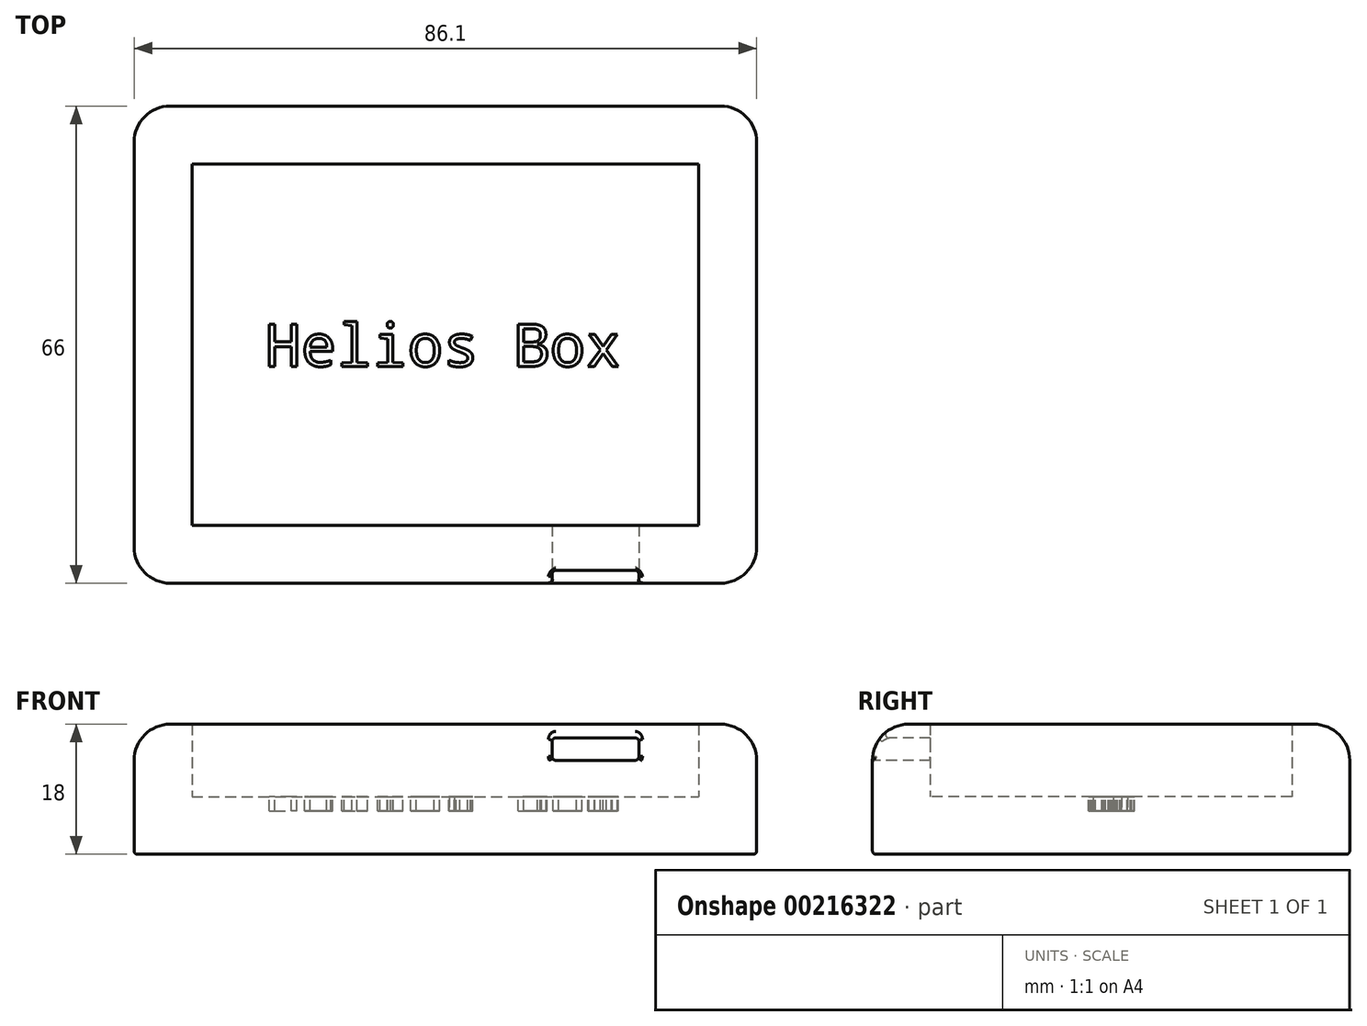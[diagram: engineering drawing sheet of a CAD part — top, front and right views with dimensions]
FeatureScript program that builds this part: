
annotation { "Feature Type Name" : "Feature", "Feature Type Description" : "" }
export const myFeature = defineFeature(function(context is Context, id is Id, definition is map)
    precondition{}
    {
        {
            var Q0;
            Q0=qCreatedBy(makeId("Top.planeOp"),FACE);
            var sketch = newSketch(context, id + "F0", { "sketchPlane" : qUnion([Q0])});
            skLineSegment(sketch, "E0.bottom", {"start": v(-35.05, 25) * mm, "end": v(35.05, 25) * mm});
            skLineSegment(sketch, "E0.top", {"start": v(-35.05, -25) * mm, "end": v(35.05, -25) * mm});
            skLineSegment(sketch, "E0.left", {"start": v(-35.05, 25) * mm, "end": v(-35.05, -25) * mm});
            skLineSegment(sketch, "E0.right", {"start": v(35.05, 25) * mm, "end": v(35.05, -25) * mm});
            skLineSegment(sketch, "E1.bottom", {"start": v(-43.05, 33) * mm, "end": v(43.05, 33) * mm});
            skLineSegment(sketch, "E1.top", {"start": v(-43.05, -33) * mm, "end": v(43.05, -33) * mm});
            skLineSegment(sketch, "E1.left", {"start": v(-43.05, 33) * mm, "end": v(-43.05, -33) * mm});
            skLineSegment(sketch, "E1.right", {"start": v(43.05, 33) * mm, "end": v(43.05, -33) * mm});
            skSolve(sketch);
        }
        {
            var Q0;
            Q0=makeQuery(id+"F0.imprint","IMPRINT",FACE,{"disambiguationData":[TD([[makeQuery(id+"F0.imprint","IMPRINT",EDGE,{"derivedFrom":sQuery(id+"F0.wireOp",EDGE,"E0.bottom")}),-1.0]])]});
            extrude(context, id + "F1", {"entities" : qUnion([Q0]), "depth" : 8 * mm});
        }
        {
            var Q0;
            Q0=makeQuery(id+"F0.imprint","IMPRINT",FACE,{"disambiguationData":[TD([[makeQuery(id+"F0.imprint","IMPRINT",EDGE,{"derivedFrom":sQuery(id+"F0.wireOp",EDGE,"E0.bottom")}),1.0]])]});
            extrude(context, id + "F2", {"entities" : qUnion([Q0]), "operationType" : NewBodyOperationType.ADD, "depth" : 18 * mm});
        }
        {
            var Q0;
            Q0=makeQuery(id+"F2.opExtrude","SWEPT_EDGE",EDGE,{"disambiguationData":[OSD([sQuery(id+"F0.wireOp",EDGE,"E1.top"),sQuery(id+"F0.wireOp",EDGE,"E1.left")])]});
            var Q1;
            Q1=makeQuery(id+"F2.opExtrude","CAP_EDGE",EDGE,{"disambiguationData":[OSD([sQuery(id+"F0.wireOp",EDGE,"E1.top")])],"isStart":false});
            var Q2;
            Q2=makeQuery(id+"F2.opExtrude","CAP_EDGE",EDGE,{"disambiguationData":[OSD([sQuery(id+"F0.wireOp",EDGE,"E1.left")])],"isStart":false});
            var Q3;
            Q3=makeQuery(id+"F2.opExtrude","SWEPT_EDGE",EDGE,{"disambiguationData":[OSD([sQuery(id+"F0.wireOp",EDGE,"E1.top"),sQuery(id+"F0.wireOp",EDGE,"E1.right")])]});
            var Q4;
            Q4=makeQuery(id+"F2.opExtrude","CAP_EDGE",EDGE,{"disambiguationData":[OSD([sQuery(id+"F0.wireOp",EDGE,"E1.right")])],"isStart":false});
            var Q5;
            Q5=makeQuery(id+"F2.opExtrude","SWEPT_EDGE",EDGE,{"disambiguationData":[OSD([sQuery(id+"F0.wireOp",EDGE,"E1.bottom"),sQuery(id+"F0.wireOp",EDGE,"E1.right")])]});
            var Q6;
            Q6=makeQuery(id+"F2.opExtrude","CAP_EDGE",EDGE,{"disambiguationData":[OSD([sQuery(id+"F0.wireOp",EDGE,"E1.bottom")])],"isStart":false});
            var Q7;
            Q7=makeQuery(id+"F2.opExtrude","SWEPT_EDGE",EDGE,{"disambiguationData":[OSD([sQuery(id+"F0.wireOp",EDGE,"E1.bottom"),sQuery(id+"F0.wireOp",EDGE,"E1.left")])]});
            fillet(context, id + "F3", {"entities" : qUnion([Q0, Q1, Q2, Q3, Q4, Q5, Q6, Q7]), "radius" : 5 * mm, "tangentPropagation" : true, "allowEdgeOverflow" : false});
        }
        {
            var Q0;
            Q0=makeQuery(id+"F2.opExtrude","SWEPT_FACE",FACE,{"disambiguationData":[OSD([sQuery(id+"F0.wireOp",EDGE,"E1.top")])]});
            var sketch = newSketch(context, id + "F4", { "sketchPlane" : qUnion([Q0])});
            skLineSegment(sketch, "E2.bottom", {"start": v(14.75, 16.1) * mm, "end": v(26.75, 16.1) * mm});
            skLineSegment(sketch, "E2.top", {"start": v(14.75, 10.6) * mm, "end": v(26.75, 10.6) * mm});
            skLineSegment(sketch, "E2.left", {"start": v(14.75, 16.1) * mm, "end": v(14.75, 10.6) * mm});
            skLineSegment(sketch, "E2.right", {"start": v(26.75, 16.1) * mm, "end": v(26.75, 10.6) * mm});
            skSolve(sketch);
        }
        {
            var Q0;
            Q0=makeQuery(id+"F4.imprint","IMPRINT",FACE,{"disambiguationData":[TD([[makeQuery(id+"F4.imprint","IMPRINT",EDGE,{"derivedFrom":sQuery(id+"F4.wireOp",EDGE,"E2.bottom")}),-1.0]])]});
            extrude(context, id + "F5", {"entities" : qUnion([Q0]), "operationType" : NewBodyOperationType.REMOVE, "oppositeDirection" : true, "depth" : 8 * mm});
        }
        {
            var Q0;
            Q0=makeQuery(id+"F5.boolean.opBoolean","INTERSECT",EDGE,{"derivedFrom":[makeQuery(id+"F3.opFillet","BLEND_FACE",FACE,{"disambiguationData":[OSD([sQuery(id+"F0.wireOp",EDGE,"E1.top")])]}),makeQuery(id+"F5.opExtrude","SWEPT_FACE",FACE,{"disambiguationData":[OSD([sQuery(id+"F4.wireOp",EDGE,"E2.bottom")])]})]});
            var Q1;
            Q1=makeQuery(id+"F5.boolean.opBoolean","INTERSECT",EDGE,{"derivedFrom":[makeQuery(id+"F3.opFillet","BLEND_FACE",FACE,{"disambiguationData":[OSD([sQuery(id+"F0.wireOp",EDGE,"E1.top")])]}),makeQuery(id+"F5.opExtrude","SWEPT_FACE",FACE,{"disambiguationData":[OSD([sQuery(id+"F4.wireOp",EDGE,"E2.right")])]})]});
            var Q2;
            Q2=makeQuery(id+"F5.boolean.opBoolean","INTERSECT",EDGE,{"derivedFrom":[makeQuery(id+"F3.opFillet","BLEND_FACE",FACE,{"disambiguationData":[OSD([sQuery(id+"F0.wireOp",EDGE,"E1.top")])]}),makeQuery(id+"F5.opExtrude","SWEPT_FACE",FACE,{"disambiguationData":[OSD([sQuery(id+"F4.wireOp",EDGE,"E2.left")])]})]});
            var Q3;
            {var subQ0=sQuery(id+"F0.wireOp",EDGE,"E1.top");Q3=makeQuery(id+"F5.boolean.opBoolean","MERGE",EDGE,{"derivedFrom":[makeQuery(id+"F3.opFillet","BLEND_EDGE",EDGE,{"blendedFrom":[makeQuery(id+"F2.opExtrude","CAP_EDGE",EDGE,{"disambiguationData":[OSD([subQ0])],"isStart":false}),makeQuery(id+"F2.opExtrude","SWEPT_FACE",FACE,{"disambiguationData":[OSD([subQ0])]})],"blendedInto":[makeQuery(id+"F2.opExtrude","SWEPT_FACE",FACE,{"disambiguationData":[OSD([subQ0])]})]}),makeQuery(id+"F5.opExtrude","CAP_EDGE",EDGE,{"disambiguationData":[OSD([subQ0])],"isStart":true})]});}
            var Q4;
            Q4=makeQuery(id+"F5.boolean.opBoolean","COPY",EDGE,{"derivedFrom":makeQuery(id+"F5.opExtrude","SWEPT_EDGE",EDGE,{"disambiguationData":[OSD([sQuery(id+"F4.wireOp",EDGE,"E2.bottom"),sQuery(id+"F4.wireOp",EDGE,"E2.right")])]})});
            var Q5;
            Q5=makeQuery(id+"F5.boolean.opBoolean","COPY",EDGE,{"derivedFrom":makeQuery(id+"F5.opExtrude","SWEPT_EDGE",EDGE,{"disambiguationData":[OSD([sQuery(id+"F0.wireOp",EDGE,"E1.top"),sQuery(id+"F4.wireOp",EDGE,"E2.right")])]})});
            var Q6;
            Q6=makeQuery(id+"F5.boolean.opBoolean","COPY",EDGE,{"derivedFrom":makeQuery(id+"F5.opExtrude","SWEPT_EDGE",EDGE,{"disambiguationData":[OSD([sQuery(id+"F0.wireOp",EDGE,"E1.top"),sQuery(id+"F4.wireOp",EDGE,"E2.left")])]})});
            var Q7;
            Q7=makeQuery(id+"F5.boolean.opBoolean","COPY",EDGE,{"derivedFrom":makeQuery(id+"F5.opExtrude","SWEPT_EDGE",EDGE,{"disambiguationData":[OSD([sQuery(id+"F4.wireOp",EDGE,"E2.bottom"),sQuery(id+"F4.wireOp",EDGE,"E2.left")])]})});
            var Q8;
            Q8=makeQuery(id+"F5.boolean.opBoolean","COPY",EDGE,{"derivedFrom":makeQuery(id+"F5.opExtrude","CAP_EDGE",EDGE,{"disambiguationData":[OSD([sQuery(id+"F0.wireOp",EDGE,"E1.top")])],"isStart":false})});
            var Q9;
            Q9=makeQuery(id+"F5.boolean.opBoolean","COPY",EDGE,{"derivedFrom":makeQuery(id+"F5.opExtrude","CAP_EDGE",EDGE,{"disambiguationData":[OSD([sQuery(id+"F4.wireOp",EDGE,"E2.left")])],"isStart":false})});
            var Q10;
            Q10=makeQuery(id+"F5.boolean.opBoolean","COPY",EDGE,{"derivedFrom":makeQuery(id+"F5.opExtrude","CAP_EDGE",EDGE,{"disambiguationData":[OSD([sQuery(id+"F4.wireOp",EDGE,"E2.bottom")])],"isStart":false})});
            var Q11;
            Q11=makeQuery(id+"F5.boolean.opBoolean","COPY",EDGE,{"derivedFrom":makeQuery(id+"F5.opExtrude","CAP_EDGE",EDGE,{"disambiguationData":[OSD([sQuery(id+"F4.wireOp",EDGE,"E2.right")])],"isStart":false})});
            fillet(context, id + "F6", {"entities" : qUnion([Q0, Q1, Q2, Q3, Q4, Q5, Q6, Q7, Q8, Q9, Q10, Q11]), "radius" : .5 * mm, "tangentPropagation" : true, "allowEdgeOverflow" : false});
        }
        {
            var Q0;
            {var subQ0=sQuery(id+"F0.wireOp",EDGE,"E0.right");var subQ1=sQuery(id+"F0.wireOp",EDGE,"E0.left");var subQ2=sQuery(id+"F0.wireOp",EDGE,"E0.top");var subQ3=sQuery(id+"F0.wireOp",EDGE,"E0.bottom");Q0=makeQuery(id+"F2.boolean.opBoolean","MERGE",FACE,{"derivedFrom":[makeQuery(id+"F1.opExtrude","CAP_FACE",FACE,{"disambiguationData":[OSD([subQ3,subQ2,subQ1,subQ0])],"isStart":true}),makeQuery(id+"F2.opExtrude","CAP_FACE",FACE,{"disambiguationData":[OSD([subQ3,subQ2,subQ1,subQ0,sQuery(id+"F0.wireOp",EDGE,"E1.bottom"),sQuery(id+"F0.wireOp",EDGE,"E1.top"),sQuery(id+"F0.wireOp",EDGE,"E1.left"),sQuery(id+"F0.wireOp",EDGE,"E1.right")])],"isStart":true})]});}
            fillet(context, id + "F7", {"entities" : qUnion([Q0]), "radius" : .5 * mm, "tangentPropagation" : true, "allowEdgeOverflow" : false});
        }
        {
            var Q0;
            Q0=makeQuery(id+"F1.opExtrude","CAP_FACE",FACE,{"disambiguationData":[OSD([sQuery(id+"F0.wireOp",EDGE,"E0.bottom"),sQuery(id+"F0.wireOp",EDGE,"E0.top"),sQuery(id+"F0.wireOp",EDGE,"E0.left"),sQuery(id+"F0.wireOp",EDGE,"E0.right")])],"isStart":false});
            var sketch = newSketch(context, id + "F8", { "sketchPlane" : qUnion([Q0])});
            skText(sketch, "E3", { "text": "Helios Box", "fontName": "DroidSansMono.ttf"});
            const initialGuessF8  = {"E3": [-0.0249, -0.00301, 1, 0, 0.0059]};
            skSetInitialGuess(sketch, initialGuessF8);
            skSolve(sketch);
        }
        {
            var Q0;
            Q0 = qSketchRegion(id + "F8", true);
            extrude(context, id + "F9", {"entities" : qUnion([Q0]), "operationType" : NewBodyOperationType.REMOVE, "oppositeDirection" : true, "depth" : 2 * mm});
        }
    });
